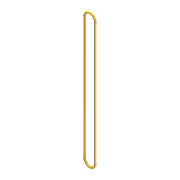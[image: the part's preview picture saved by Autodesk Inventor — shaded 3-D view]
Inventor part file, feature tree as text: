
AUTODESK INVENTOR PART (.ipt)
format: ipt  version: 2012 (Build 160160000, 160)  size: 86,016 bytes
history: native  units: in
note: dims shown in document units (in); Inventor stores cm internally (conversion verified against a paired STEP export)
features: extrude x1, fillet x1, sketch x1
ambient origin geometry x8: Origin, YZ Plane, XZ Plane, XY Plane, X Axis, Y Axis, Z Axis, Center Point
bodies: Solid1 (feature_tree)
feature tree (3):
  extrude  "Extrusion1"  Depth=0.75in
  fillet  "Fillet1"  Radius=0.1875in
  sketch  "Sketch1"  dims[d0=18.5in d1=0.75in d2=0.1875in d3=0.1875in d4=0.0in d5=0.0938in]
